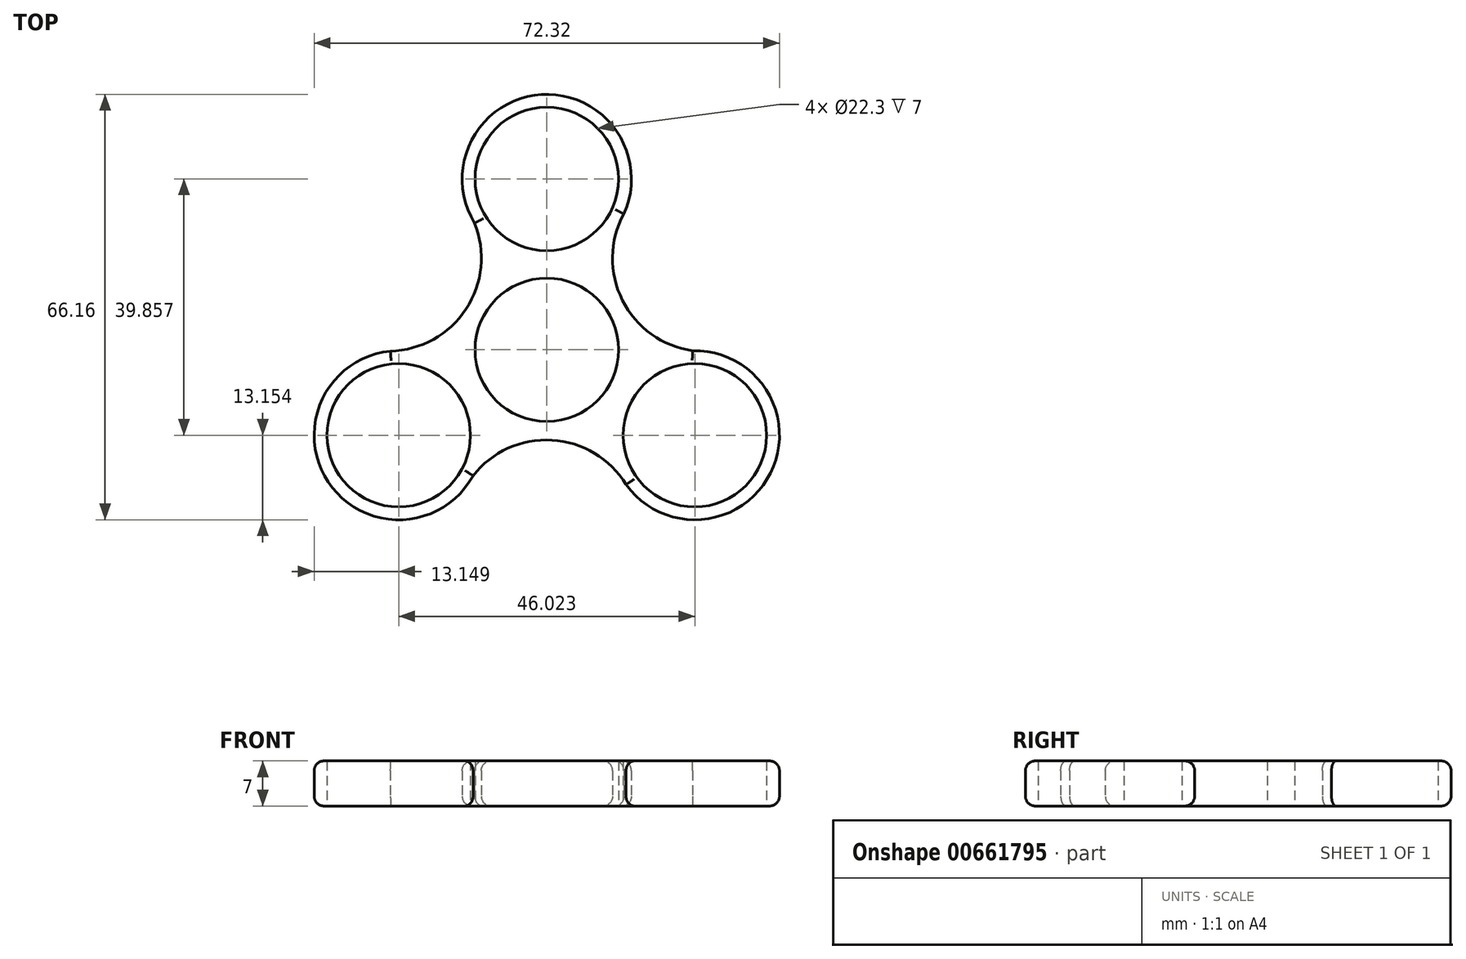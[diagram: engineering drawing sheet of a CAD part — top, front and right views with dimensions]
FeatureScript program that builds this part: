
annotation { "Feature Type Name" : "Feature", "Feature Type Description" : "" }
export const myFeature = defineFeature(function(context is Context, id is Id, definition is map)
    precondition{}
    {
        {
            var Q0;
            Q0=qCreatedBy(makeId("Top.planeOp"),FACE);
            var sketch = newSketch(context, id + "F0", { "sketchPlane" : qUnion([Q0])});
            skCircle(sketch, "E0", {"center": v(0, 0) * mm, "radius": 11.15 * mm});
            skCircle(sketch, "E1", {"center": v(0, 26.57) * mm, "radius": 11.15 * mm});
            skArc(sketch, "E2", {"start": v(11.53, 20.25) * mm, "mid": v(-0.3, 39.72) * mm, "end": v(-11.22, 19.72) * mm});
            skCircle(sketch, "E3.1.0", {"center": v(-23.01, -13.29) * mm, "radius": 11.15 * mm});
            skArc(sketch, "E3.1.1", {"start": v(-23.3, -0.14) * mm, "mid": v(-34.24, -20.13) * mm, "end": v(-11.47, -19.58) * mm});
            skCircle(sketch, "E3.2.0", {"center": v(23.01, -13.29) * mm, "radius": 11.15 * mm});
            skArc(sketch, "E3.2.1", {"start": v(11.77, -20.11) * mm, "mid": v(34.55, -19.6) * mm, "end": v(22.69, -0.14) * mm});
            skArc(sketch, "E4", {"start": v(11.98, 21.15) * mm, "mid": v(11.77, 7.7) * mm, "end": v(22.69, -0.14) * mm});
            skArc(sketch, "E5.1.0", {"start": v(-24.3, -0.2) * mm, "mid": v(-12.55, 6.34) * mm, "end": v(-11.22, 19.72) * mm});
            skArc(sketch, "E5.2.0", {"start": v(12.32, -20.95) * mm, "mid": v(0.79, -14.04) * mm, "end": v(-11.47, -19.58) * mm});
            skSolve(sketch);
        }
        {
            var Q0;
            Q0=makeQuery(id+"F0.imprint","IMPRINT",FACE,{"disambiguationData":[TD([[makeQuery(id+"F0.imprint","IMPRINT",EDGE,{"derivedFrom":sQuery(id+"F0.wireOp",EDGE,"E0")}),-1.0]])]});
            extrude(context, id + "F1", {"entities" : qUnion([Q0]), "depth" : 7 * mm, "offsetDistance" : 25 * mm});
        }
        {
            var Q0;
            Q0=makeQuery(id+"F1.opExtrude","CAP_EDGE",EDGE,{"disambiguationData":[OSD([sQuery(id+"F0.wireOp",EDGE,"E3.1.1")])],"isStart":false});
            var Q1;
            Q1=makeQuery(id+"F1.opExtrude","CAP_EDGE",EDGE,{"disambiguationData":[OSD([sQuery(id+"F0.wireOp",EDGE,"E5.1.0")])],"isStart":false});
            var Q2;
            Q2=makeQuery(id+"F1.opExtrude","CAP_EDGE",EDGE,{"disambiguationData":[OSD([sQuery(id+"F0.wireOp",EDGE,"E2")])],"isStart":false});
            var Q3;
            Q3=makeQuery(id+"F1.opExtrude","CAP_EDGE",EDGE,{"disambiguationData":[OSD([sQuery(id+"F0.wireOp",EDGE,"E4")])],"isStart":false});
            var Q4;
            Q4=makeQuery(id+"F1.opExtrude","CAP_EDGE",EDGE,{"disambiguationData":[OSD([sQuery(id+"F0.wireOp",EDGE,"E3.2.1")])],"isStart":false});
            var Q5;
            Q5=makeQuery(id+"F1.opExtrude","CAP_EDGE",EDGE,{"disambiguationData":[OSD([sQuery(id+"F0.wireOp",EDGE,"E5.2.0")])],"isStart":false});
            var Q6;
            Q6=makeQuery(id+"F1.opExtrude","CAP_EDGE",EDGE,{"disambiguationData":[OSD([sQuery(id+"F0.wireOp",EDGE,"E3.1.1")])],"isStart":true});
            var Q7;
            Q7=makeQuery(id+"F1.opExtrude","CAP_EDGE",EDGE,{"disambiguationData":[OSD([sQuery(id+"F0.wireOp",EDGE,"E5.2.0")])],"isStart":true});
            var Q8;
            Q8=makeQuery(id+"F1.opExtrude","CAP_EDGE",EDGE,{"disambiguationData":[OSD([sQuery(id+"F0.wireOp",EDGE,"E3.2.1")])],"isStart":true});
            var Q9;
            Q9=makeQuery(id+"F1.opExtrude","CAP_EDGE",EDGE,{"disambiguationData":[OSD([sQuery(id+"F0.wireOp",EDGE,"E5.1.0")])],"isStart":true});
            var Q10;
            Q10=makeQuery(id+"F1.opExtrude","CAP_EDGE",EDGE,{"disambiguationData":[OSD([sQuery(id+"F0.wireOp",EDGE,"E2")])],"isStart":true});
            var Q11;
            Q11=makeQuery(id+"F1.opExtrude","CAP_EDGE",EDGE,{"disambiguationData":[OSD([sQuery(id+"F0.wireOp",EDGE,"E4")])],"isStart":true});
            fillet(context, id + "F2", {"entities" : qUnion([Q0, Q1, Q2, Q3, Q4, Q5, Q6, Q7, Q8, Q9, Q10, Q11]), "radius" : 1.5 * mm, "tangentPropagation" : true, "allowEdgeOverflow" : false});
        }
    });
